# Revit family: xToilet_Elongated-Right_Height-American_Standard-Acticlean-714AA.154
name_source: partatom
category: Plumbing Fixtures
revit_build: Autodesk Revit 2014 (Build: 20130308_1515(x64)
units: mm (PartAtom-declared; Revit-internal decimal feet)

## types (1)
- 714AA.154
    ADA Compliant = Yes
    Assembly Code = D2010110
    Bowl Shape = Elongated
    CW Connection = Yes
    CWFU = 5
    Cold Water Connection Diameter = 1/2"
    Cold Water Connection Height = 10"
    Cold Water Connection Radius = 1/4"
    Default Elevation = 16 1/2"
    Description = Acticlean HET Right Height Elongated Complete Toilet
    Flush Rate = 1.28 Gpm (4.8 Lpf)
    HW Connection = No
    HWFU = 0
    Height = 31 3/8"
    High-Efficiency = Yes
    Installation Type = Floor Mounted
    Length = 30 3/16"
    Manufacturer = American Standard
    Material = Vitreous China-American Standard-020-White
    Model = 714AA.154
    Price = Prices may vary. Please consult Manufacturer Representative for most up-to-date price list.
    URL = http://www.americanstandard-us.com
    Vent Connection = No
    WFU = 5
    Warranty Information = Lifetime warranty on chinaware, 10 year warranty on mechanical parts, 1 year on electronics and 1 year warranty on seat.
    Waste Connection = Yes
    Waste Connection Diameter = 2 1/16"
    Waste Connection Radius = 1 1/32"
    Width = 20 11/16"

## geometry (parser evidence)
native form markers: Sweep x2
no freeform markers — native parametric forms only
